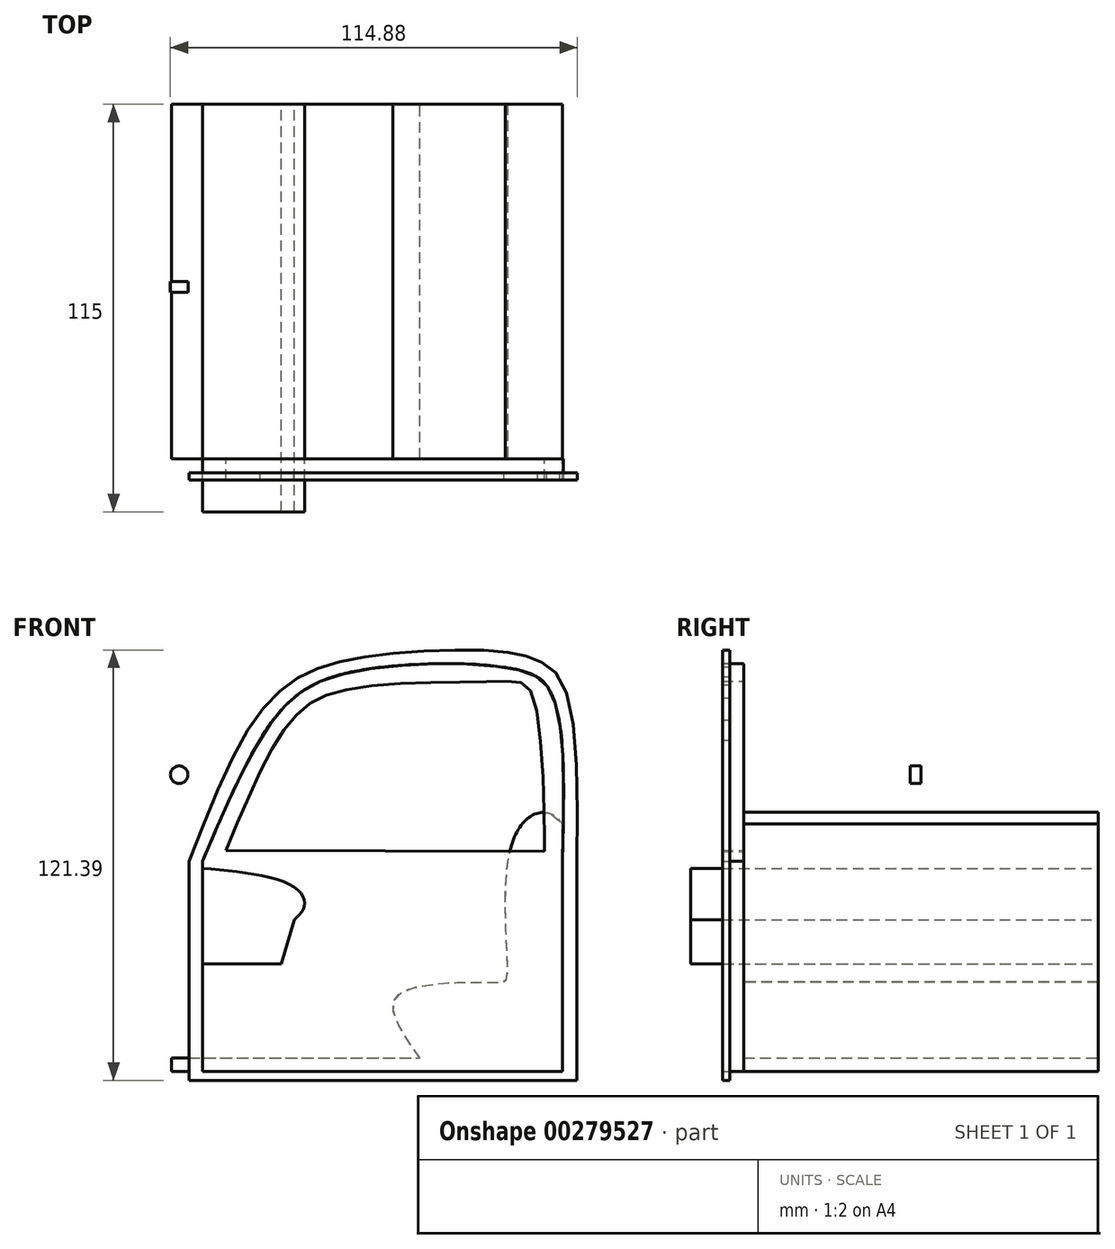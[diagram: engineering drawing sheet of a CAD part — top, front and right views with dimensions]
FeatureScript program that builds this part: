
annotation { "Feature Type Name" : "Feature", "Feature Type Description" : "" }
export const myFeature = defineFeature(function(context is Context, id is Id, definition is map)
    precondition{}
    {
        {
            var Q0;
            Q0=qCreatedBy(makeId("Front.planeOp"),FACE);
            var sketch = newSketch(context, id + "F0", { "sketchPlane" : qUnion([Q0])});
            skLineSegment(sketch, "E0.bottom", {"start": v(-52.37, -30.32) * mm, "end": v(58, -30.32) * mm});
            skLineSegment(sketch, "E0.top", {"start": v(-52.37, 75.93) * mm, "end": v(58, 75.93) * mm});
            skLineSegment(sketch, "E0.left", {"start": v(-52.37, -30.32) * mm, "end": v(-52.37, 75.93) * mm});
            skLineSegment(sketch, "E0.right", {"start": v(58, -30.32) * mm, "end": v(58, 75.93) * mm});
            skLineSegment(sketch, "E1", {"start": v(-52.37, -26.56) * mm, "end": v(17.83, -26.56) * mm});
            skFitSpline(sketch, "E2", {"points": [v(17.83, -26.56) * mm, v(11.64, -8.73) * mm, v(39.8, -5.16) * mm, v(42.43, -3.66) * mm, v(45.05, 37.08) * mm, v(58, 39.52) * mm, v(58, 9.86) * mm], "startDerivative": vector(-102.72, 146.21) * mm, "endDerivative": vector(-61.38, 44.33) * mm});
            skSolve(sketch);
        }
        {
            var Q0;
            {var subQ2=sQuery(id+"F0.wireOp",EDGE,"E0.bottom");Q0=makeQuery(id+"F0.imprint","IMPRINT",FACE,{"disambiguationData":[TD([[makeQuery(id+"F0.imprint","IMPRINT",EDGE,{"derivedFrom":subQ2}),1.0]])]});}
            extrude(context, id + "F1", {"entities" : qUnion([Q0]), "endBound" : BoundingType.SYMMETRIC, "depth" : 100 * mm});
        }
        {
            var Q0;
            Q0=makeQuery(id+"F1.opExtrude","CAP_FACE",FACE,{"disambiguationData":[OSD([sQuery(id+"F0.wireOp",EDGE,"E0.bottom"),sQuery(id+"F0.wireOp",EDGE,"E0.left"),sQuery(id+"F0.wireOp",EDGE,"E0.right"),sQuery(id+"F0.wireOp",EDGE,"E1"),sQuery(id+"F0.wireOp",EDGE,"E2")])],"isStart":true});
            var sketch = newSketch(context, id + "F2", { "sketchPlane" : qUnion([Q0])});
            skLineSegment(sketch, "E3.bottom", {"start": v(-35.3, -30.32) * mm, "end": v(30.41, -30.32) * mm});
            skLineSegment(sketch, "E3.top", {"start": v(-35.3, 0) * mm, "end": v(21.37, 0) * mm});
            skLineSegment(sketch, "E3.left", {"start": v(-35.3, -30.32) * mm, "end": v(-35.3, 0) * mm});
            skLineSegment(sketch, "E4", {"start": v(21.37, 0) * mm, "end": v(17.65, 12.48) * mm});
            skFitSpline(sketch, "E5", {"points": [v(17.65, 12.48) * mm, v(14.83, 16.43) * mm, v(17.65, 21.68) * mm, v(43.55, 26.94) * mm, v(64.2, 27.5) * mm], "startDerivative": vector(-24.47, 23.82) * mm, "endDerivative": vector(59, 0.05) * mm});
            skLineSegment(sketch, "E6", {"start": v(43.55, 26.94) * mm, "end": v(43.55, -30.32) * mm});
            skLineSegment(sketch, "E7", {"start": v(43.55, -30.32) * mm, "end": v(30.41, -30.32) * mm});
            skPoint(sketch, "E3.right.end.orphan", {"position": v(30.41, 0) * mm});
            skLineSegment(sketch, "E8", {"start": v(21.37, 0) * mm, "end": v(43.55, 0) * mm});
            skSolve(sketch);
        }
        {
            var Q0;
            Q0=makeQuery(id+"F2.imprint","IMPRINT",FACE,{"disambiguationData":[TD([[makeQuery(id+"F2.imprint","IMPRINT",EDGE,{"derivedFrom":sQuery(id+"F2.wireOp",EDGE,"E4")}),-1.0]])]});
            extrude(context, id + "F3", {"entities" : qUnion([Q0]), "oppositeDirection" : true, "depth" : 115 * mm});
        }
        {
            var Q0;
            Q0=makeQuery(id+"F1.opExtrude","CAP_FACE",FACE,{"disambiguationData":[OSD([sQuery(id+"F0.wireOp",EDGE,"E0.bottom"),sQuery(id+"F0.wireOp",EDGE,"E0.left"),sQuery(id+"F0.wireOp",EDGE,"E0.right"),sQuery(id+"F0.wireOp",EDGE,"E1"),sQuery(id+"F0.wireOp",EDGE,"E2")])],"isStart":false});
            var sketch = newSketch(context, id + "F4", { "sketchPlane" : qUnion([Q0])});
            skLineSegment(sketch, "E9.bottom", {"start": v(58, -30.32) * mm, "end": v(-43.55, -30.32) * mm});
            skLineSegment(sketch, "E9.left", {"start": v(58, -30.32) * mm, "end": v(58, 29) * mm});
            skLineSegment(sketch, "E9.right", {"start": v(-43.55, -30.32) * mm, "end": v(-43.55, 29) * mm});
            skFitSpline(sketch, "E10", {"points": [v(-43.55, 29) * mm, v(-22.9, 69.74) * mm, v(-1.88, 82.32) * mm, v(43.36, 83.44) * mm, v(55.2, 75.75) * mm, v(58, 29) * mm], "startDerivative": vector(85.44, 201.79) * mm, "endDerivative": vector(-6.45, -241.46) * mm});
            skFitSpline(sketch, "E11", {"points": [v(-36.92, 32) * mm, v(-19.34, 67.67) * mm, v(-1.88, 77.62) * mm, v(40.92, 79.69) * mm, v(49.75, 75.37) * mm, v(52.94, 31.82) * mm, v(52.94, 31.63) * mm], "startDerivative": vector(74.67, 181.05) * mm, "endDerivative": vector(0.05, -3.93) * mm});
            skLineSegment(sketch, "E12", {"start": v(-36.92, 32) * mm, "end": v(52.94, 31.82) * mm});
            skSolve(sketch);
        }
        {
            var Q0;
            Q0=qSketchRegion(id+"F4",true);
            extrude(context, id + "F5", {"entities" : qUnion([Q0]), "depth" : 6 * mm});
        }
        {
            var Q0;
            Q0=makeQuery(id+"F5.opExtrude","CAP_FACE",FACE,{"disambiguationData":[OSD([sQuery(id+"F4.wireOp",EDGE,"E9.bottom"),sQuery(id+"F4.wireOp",EDGE,"E9.left"),sQuery(id+"F4.wireOp",EDGE,"E9.right"),sQuery(id+"F4.wireOp",EDGE,"E10"),sQuery(id+"F4.wireOp",EDGE,"E11"),sQuery(id+"F4.wireOp",EDGE,"E12")])],"isStart":false});
            var sketch = newSketch(context, id + "F6", { "sketchPlane" : qUnion([Q0])});
            skLineSegment(sketch, "E13.top", {"start": v(-47.37, -32.82) * mm, "end": v(62.16, -32.82) * mm});
            skLineSegment(sketch, "E13.left", {"start": v(-47.37, 29) * mm, "end": v(-47.37, -32.82) * mm});
            skLineSegment(sketch, "E13.right", {"start": v(62.16, 29) * mm, "end": v(62.16, -32.82) * mm});
            skFitSpline(sketch, "E14", {"points": [v(-47.37, 29) * mm, v(-31.58, 64.72) * mm, v(-19.39, 78.91) * mm, v(-6.2, 84.9) * mm, v(16.79, 88.1) * mm, v(41.38, 88.1) * mm, v(50.97, 85.7) * mm, v(58.39, 78.67) * mm, v(62.16, 29) * mm], "startDerivative": vector(92.74, 238.3) * mm, "endDerivative": vector(-2.8, -324.84) * mm});
            skLineSegment(sketch, "E15.top", {"start": v(-43.55, -30.32) * mm, "end": v(58, -30.32) * mm});
            skLineSegment(sketch, "E15.left", {"start": v(-43.55, 29) * mm, "end": v(-43.55, -30.32) * mm});
            skLineSegment(sketch, "E15.right", {"start": v(58, 29) * mm, "end": v(58, -30.32) * mm});
            skFitSpline(sketch, "E16", {"points": [v(-43.55, 29) * mm, v(-27.48, 63) * mm, v(-17.96, 74.99) * mm, v(-6.2, 81.2) * mm, v(16.79, 84.53) * mm, v(41.38, 83.75) * mm, v(50.97, 80.93) * mm, v(53.48, 78.67) * mm, v(57.1, 68.74) * mm, v(58, 29) * mm], "startDerivative": vector(103.55, 237.38) * mm, "endDerivative": vector(-7.28, -274.99) * mm});
            skSolve(sketch);
        }
        {
            var Q0;
            Q0=makeQuery(id+"F6.imprint","IMPRINT",FACE,{"disambiguationData":[TD([[makeQuery(id+"F6.imprint","IMPRINT",EDGE,{"derivedFrom":sQuery(id+"F6.wireOp",EDGE,"E13.top")}),1.0]])]});
            var Q1;
            Q1=sQuery(id+"F6.wireOp",EDGE,"E14");
            var Q2;
            Q2=sQuery(id+"F6.wireOp",EDGE,"E16");
            var Q3;
            Q3=sQuery(id+"F6.wireOp",EDGE,"E15.right");
            var Q4;
            Q4=sQuery(id+"F6.wireOp",EDGE,"E13.right");
            var Q5;
            Q5=sQuery(id+"F6.wireOp",EDGE,"E15.top");
            var Q6;
            Q6=sQuery(id+"F6.wireOp",EDGE,"E13.top");
            var Q7;
            Q7=sQuery(id+"F6.wireOp",EDGE,"E13.left");
            var Q8;
            Q8=sQuery(id+"F6.wireOp",EDGE,"E15.left");
            extrude(context, id + "F7", {"entities" : qUnion([Q0]), "surfaceEntities" : qUnion([Q1, Q2, Q3, Q4, Q5, Q6, Q7, Q8]), "oppositeDirection" : true, "depth" : 2 * mm});
        }
        {
            var Q0;
            Q0=qCreatedBy(makeId("Front.planeOp"),FACE);
            var sketch = newSketch(context, id + "F8", { "sketchPlane" : qUnion([Q0])});
            skCircle(sketch, "E17", {"center": v(-50.16, 53.39) * mm, "radius": 2.48 * mm});
            skSolve(sketch);
        }
        {
            var Q0;
            Q0=qSketchRegion(id+"F8",true);
            extrude(context, id + "F9", {"entities" : qUnion([Q0]), "depth" : 3 * mm});
        }
    });
